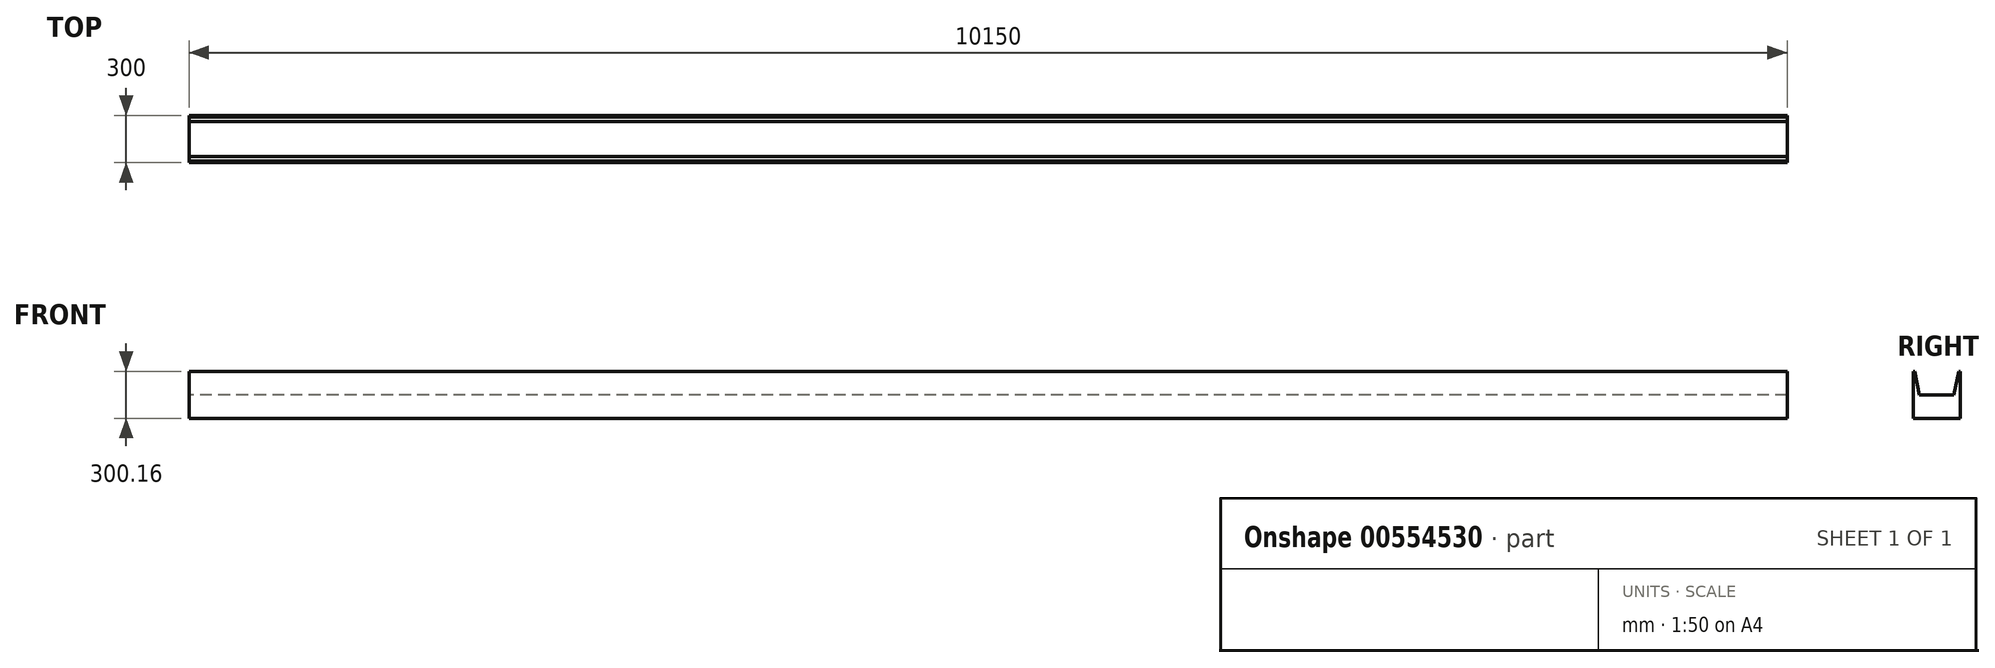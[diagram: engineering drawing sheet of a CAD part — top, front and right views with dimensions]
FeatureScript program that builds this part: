
annotation { "Feature Type Name" : "Feature", "Feature Type Description" : "" }
export const myFeature = defineFeature(function(context is Context, id is Id, definition is map)
    precondition{}
    {
        {
            var Q0;
            Q0=qCreatedBy(makeId("Right.planeOp"),FACE);
            var sketch = newSketch(context, id + "F0", { "sketchPlane" : qUnion([Q0])});
            skLineSegment(sketch, "E0", {"start": v(-13.86, 0) * mm, "end": v(286.14, 0) * mm});
            skLineSegment(sketch, "E1", {"start": v(286.14, 0) * mm, "end": v(286.14, 300.16) * mm});
            skLineSegment(sketch, "E2", {"start": v(245.97, 149.98) * mm, "end": v(25.87, 149.98) * mm});
            skLineSegment(sketch, "E3", {"start": v(-13.83, 300.16) * mm, "end": v(-13.86, 0) * mm});
            skLineSegment(sketch, "E4", {"start": v(286.14, 300.16) * mm, "end": v(275.83, 300.16) * mm});
            skLineSegment(sketch, "E5", {"start": v(275.83, 300.16) * mm, "end": v(245.97, 149.98) * mm});
            skLineSegment(sketch, "E6", {"start": v(-13.83, 300.16) * mm, "end": v(-3.36, 300.16) * mm});
            skLineSegment(sketch, "E7", {"start": v(-3.36, 300.16) * mm, "end": v(25.87, 149.98) * mm});
            skSolve(sketch);
        }
        {
            var Q0;
            Q0=makeQuery(id+"F0.imprint","IMPRINT",FACE,{"disambiguationData":[TD([[makeQuery(id+"F0.imprint","IMPRINT",EDGE,{"derivedFrom":sQuery(id+"F0.wireOp",EDGE,"E0")}),1.0]])]});
            extrude(context, id + "F1", {"entities" : qUnion([Q0]), "depth" : 10150 * mm, "offsetDistance" : 25 * mm});
        }
    });
